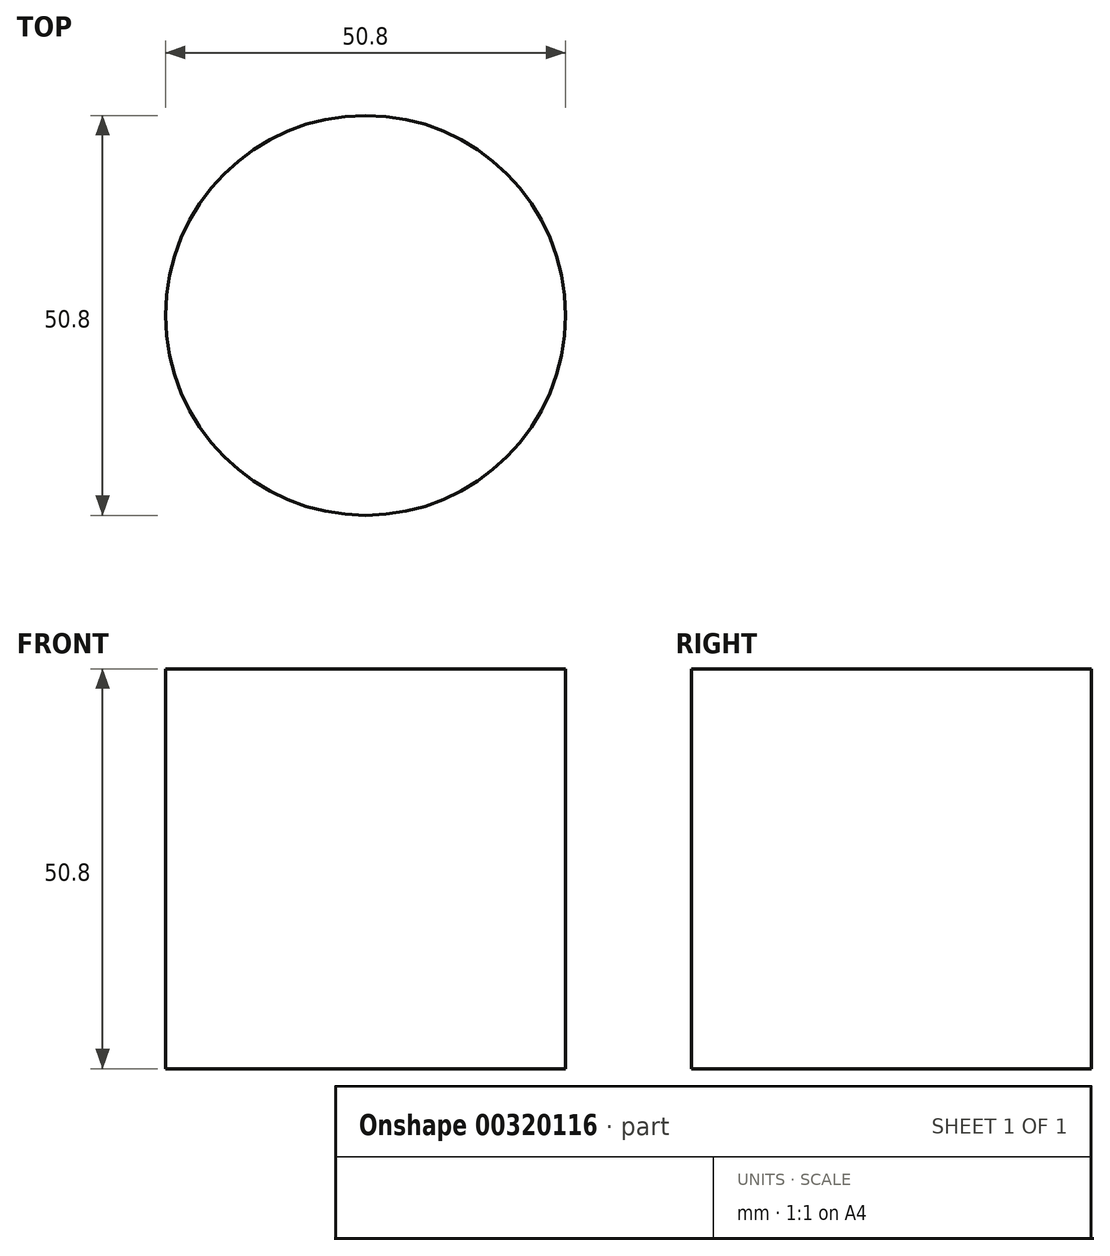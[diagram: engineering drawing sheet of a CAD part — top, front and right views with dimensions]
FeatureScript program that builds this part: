
annotation { "Feature Type Name" : "Feature", "Feature Type Description" : "" }
export const myFeature = defineFeature(function(context is Context, id is Id, definition is map)
    precondition{}
    {
        {
            var Q0;
            Q0=qCreatedBy(makeId("Top.planeOp"),FACE);
            var sketch = newSketch(context, id + "F0", { "sketchPlane" : qUnion([Q0])});
            skCircle(sketch, "E0", {"center": v(0, 0) * mm, "radius": 25.4 * mm});
            skSolve(sketch);
        }
        {
            var Q0;
            Q0 = qSketchRegion(id + "F0", true);
            extrude(context, id + "F1", {"entities" : qUnion([Q0]), "depth" : 50.8 * mm});
        }
    });
